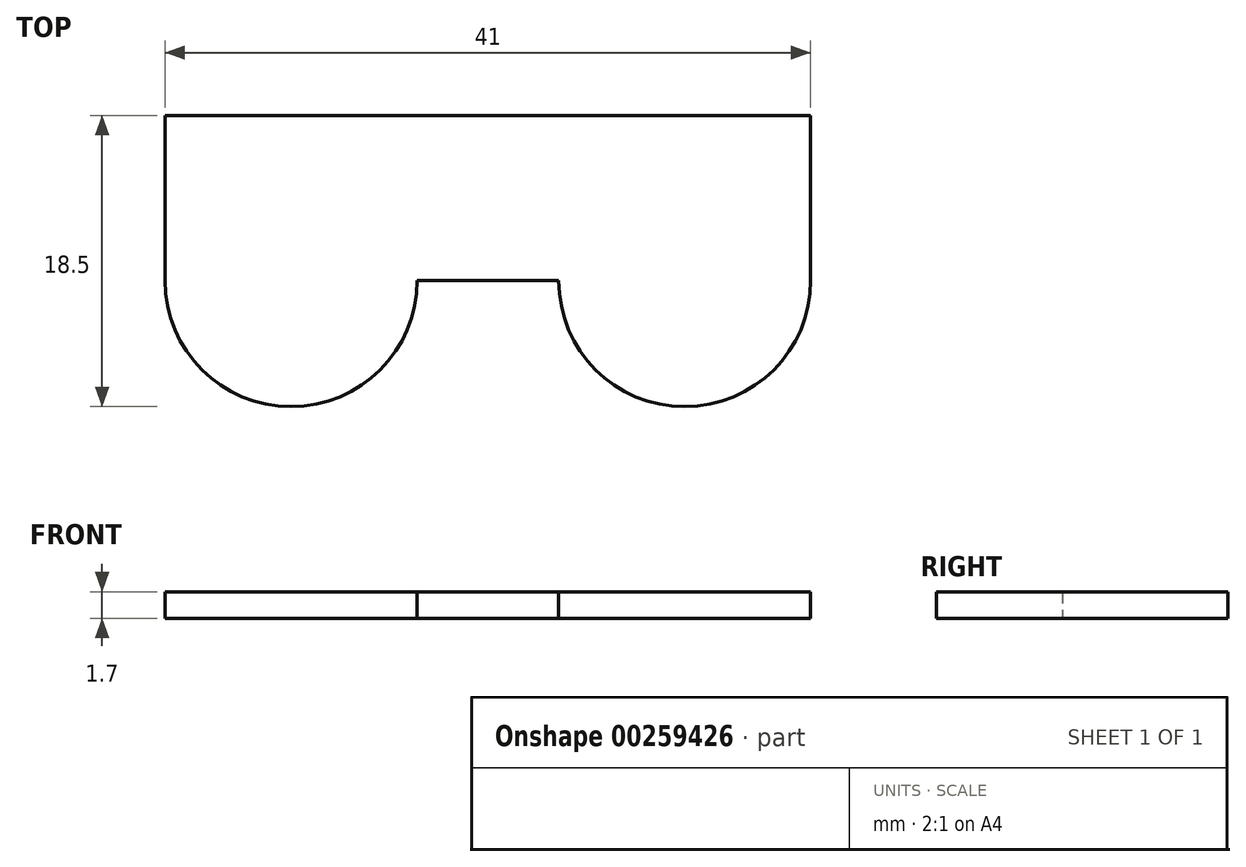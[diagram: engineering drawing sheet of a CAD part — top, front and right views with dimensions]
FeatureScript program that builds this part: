
annotation { "Feature Type Name" : "Feature", "Feature Type Description" : "" }
export const myFeature = defineFeature(function(context is Context, id is Id, definition is map)
    precondition{}
    {
        {
            var Q0;
            Q0=qCreatedBy(makeId("Top.planeOp"),FACE);
            var sketch = newSketch(context, id + "F0", { "sketchPlane" : qUnion([Q0])});
            skLineSegment(sketch, "E0", {"start": v(4.5, -16) * mm, "end": v(-4.5, -16) * mm});
            skArc(sketch, "E1", {"start": v(-20.5, -16) * mm, "mid": v(-12.5, -24) * mm, "end": v(-4.5, -16) * mm});
            skArc(sketch, "E2", {"start": v(4.5, -16) * mm, "mid": v(12.5, -24) * mm, "end": v(20.5, -16) * mm});
            skLineSegment(sketch, "E3", {"start": v(-20.5, -16) * mm, "end": v(-20.5, -5.5) * mm});
            skLineSegment(sketch, "E4", {"start": v(20.5, -16) * mm, "end": v(20.5, -5.5) * mm});
            skLineSegment(sketch, "E5", {"start": v(-20.5, -5.5) * mm, "end": v(20.5, -5.5) * mm});
            skPoint(sketch, "E6.orphan", {"position": v(20.5, 0) * mm});
            skPoint(sketch, "E7.orphan", {"position": v(-20.5, 0) * mm});
            skSolve(sketch);
        }
        {
            var Q0;
            Q0 = qSketchRegion(id + "F0", true);
            extrude(context, id + "F1", {"entities" : qUnion([Q0]), "depth" : 1.7 * mm});
        }
    });
